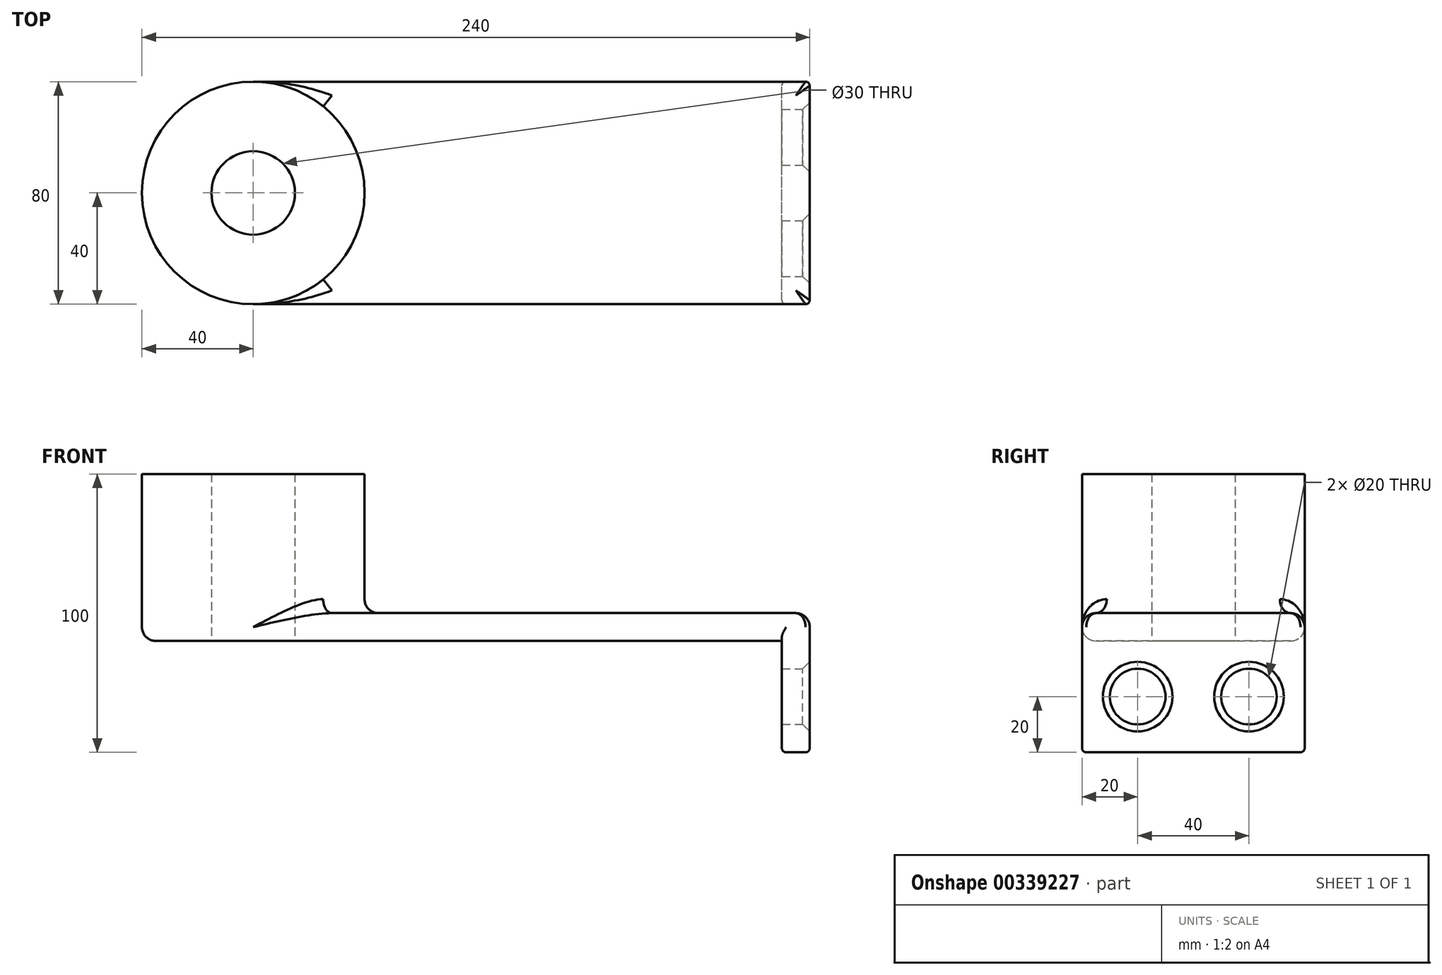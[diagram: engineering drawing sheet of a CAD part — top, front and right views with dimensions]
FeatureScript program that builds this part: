
annotation { "Feature Type Name" : "Feature", "Feature Type Description" : "" }
export const myFeature = defineFeature(function(context is Context, id is Id, definition is map)
    precondition{}
    {
        {
            var Q0;
            Q0=qCreatedBy(makeId("Top.planeOp"),FACE);
            var sketch = newSketch(context, id + "F0", { "sketchPlane" : qUnion([Q0])});
            skLineSegment(sketch, "E0.bottom", {"start": v(100, 40) * mm, "end": v(-100, 40) * mm});
            skLineSegment(sketch, "E0.top", {"start": v(100, -40) * mm, "end": v(-100, -40) * mm});
            skLineSegment(sketch, "E0.left", {"start": v(100, 40) * mm, "end": v(100, -40) * mm});
            skLineSegment(sketch, "E0.right", {"start": v(-100, 40) * mm, "end": v(-100, -40) * mm});
            skPoint(sketch, "E0.middle", {"position": v(0, 0) * mm});
            skCircle(sketch, "E1", {"center": v(-100, 0) * mm, "radius": 40 * mm});
            skCircle(sketch, "E2", {"center": v(-100, 0) * mm, "radius": 15 * mm});
            skSolve(sketch);
        }
        {
            var Q0;
            Q0=makeQuery(id+"F0.imprint","IMPRINT",FACE,{"disambiguationData":[TD([[makeQuery(id+"F0.imprint","IMPRINT",EDGE,{"derivedFrom":sQuery(id+"F0.wireOp",EDGE,"E0.bottom")}),1.0]])]});
            var Q1;
            {var subQ1=sQuery(id+"F0.wireOp",EDGE,"E0.right");var subQ3=sQuery(id+"F0.wireOp",EDGE,"E2");var subQ4=makeQuery(id+"F0.imprint","INTERSECT",VERTEX,{"disambiguationData":[OD(0.0)],"derivedFrom":[subQ1,subQ3]});Q1=makeQuery(id+"F0.imprint","IMPRINT",FACE,{"disambiguationData":[TD([[makeQuery(id+"F0.imprint","IMPRINT",EDGE,{"disambiguationData":[TD([[subQ4,1.0]])],"derivedFrom":subQ3}),-1.0]])]});}
            var Q2;
            {var subQ1=sQuery(id+"F0.wireOp",EDGE,"E0.right");var subQ3=sQuery(id+"F0.wireOp",EDGE,"E2");var subQ4=makeQuery(id+"F0.imprint","INTERSECT",VERTEX,{"disambiguationData":[OD(0.0)],"derivedFrom":[subQ1,subQ3]});Q2=makeQuery(id+"F0.imprint","IMPRINT",FACE,{"disambiguationData":[TD([[makeQuery(id+"F0.imprint","IMPRINT",EDGE,{"disambiguationData":[TD([[subQ4,-1.0]])],"derivedFrom":subQ3}),-1.0]])]});}
            extrude(context, id + "F1", {"entities" : qUnion([Q0, Q1, Q2]), "depth" : 10 * mm});
        }
        {
            var Q0;
            Q0=makeQuery(id+"F1.opExtrude","SWEPT_FACE",FACE,{"disambiguationData":[OSD([sQuery(id+"F0.wireOp",EDGE,"E0.left")])]});
            var sketch = newSketch(context, id + "F2", { "sketchPlane" : qUnion([Q0])});
            skLineSegment(sketch, "E3.bottom", {"start": v(-40, 10) * mm, "end": v(40, 10) * mm});
            skLineSegment(sketch, "E3.top", {"start": v(-40, -40) * mm, "end": v(40, -40) * mm});
            skLineSegment(sketch, "E3.left", {"start": v(-40, 10) * mm, "end": v(-40, -40) * mm});
            skLineSegment(sketch, "E3.right", {"start": v(40, 10) * mm, "end": v(40, -40) * mm});
            skCircle(sketch, "E4", {"center": v(-20, -20) * mm, "radius": 10 * mm});
            skCircle(sketch, "E5", {"center": v(20, -20) * mm, "radius": 10 * mm});
            skLineSegment(sketch, "E6", {"start": v(0, -40) * mm, "end": v(0, 10) * mm, "construction": true});
            skSolve(sketch);
        }
        {
            var Q0;
            Q0 = qSketchRegion(id + "F2", true);
            extrude(context, id + "F3", {"entities" : qUnion([Q0]), "operationType" : NewBodyOperationType.ADD, "oppositeDirection" : true, "depth" : 10 * mm});
        }
        {
            var Q0;
            {var subQ1=sQuery(id+"F0.wireOp",EDGE,"E0.right");var subQ3=sQuery(id+"F0.wireOp",EDGE,"E2");var subQ4=makeQuery(id+"F0.imprint","INTERSECT",VERTEX,{"disambiguationData":[OD(0.0)],"derivedFrom":[subQ1,subQ3]});Q0=makeQuery(id+"F0.imprint","IMPRINT",FACE,{"disambiguationData":[TD([[makeQuery(id+"F0.imprint","IMPRINT",EDGE,{"disambiguationData":[TD([[subQ4,1.0]])],"derivedFrom":subQ3}),-1.0]])]});}
            var Q1;
            {var subQ1=sQuery(id+"F0.wireOp",EDGE,"E0.right");var subQ3=sQuery(id+"F0.wireOp",EDGE,"E2");var subQ4=makeQuery(id+"F0.imprint","INTERSECT",VERTEX,{"disambiguationData":[OD(0.0)],"derivedFrom":[subQ1,subQ3]});Q1=makeQuery(id+"F0.imprint","IMPRINT",FACE,{"disambiguationData":[TD([[makeQuery(id+"F0.imprint","IMPRINT",EDGE,{"disambiguationData":[TD([[subQ4,-1.0]])],"derivedFrom":subQ3}),-1.0]])]});}
            extrude(context, id + "F4", {"entities" : qUnion([Q0, Q1]), "operationType" : NewBodyOperationType.ADD, "depth" : 60 * mm});
        }
        {
            var Q0;
            Q0=makeQuery(id+"F1.opExtrude","CAP_EDGE",EDGE,{"disambiguationData":[OSD([sQuery(id+"F0.wireOp",EDGE,"E0.left")])],"isStart":false});
            var Q1;
            {var subQ0=sQuery(id+"F0.wireOp",EDGE,"E1");Q1=makeQuery(id+"F4.boolean.opBoolean","INTERSECT",EDGE,{"derivedFrom":[makeQuery(id+"F1.opExtrude","CAP_FACE",FACE,{"disambiguationData":[OSD([sQuery(id+"F0.wireOp",EDGE,"E0.bottom"),sQuery(id+"F0.wireOp",EDGE,"E0.top"),sQuery(id+"F0.wireOp",EDGE,"E0.left"),subQ0,sQuery(id+"F0.wireOp",EDGE,"E2")])],"isStart":false}),makeQuery(id+"F4.opExtrude","SWEPT_FACE",FACE,{"disambiguationData":[OSD([subQ0])]})]});}
            var Q2;
            Q2=makeQuery(id+"F1.opExtrude","CAP_EDGE",EDGE,{"disambiguationData":[OSD([sQuery(id+"F0.wireOp",EDGE,"E0.top")])],"isStart":false});
            var Q3;
            Q3=makeQuery(id+"F1.opExtrude","CAP_EDGE",EDGE,{"disambiguationData":[OSD([sQuery(id+"F0.wireOp",EDGE,"E0.bottom")])],"isStart":false});
            var Q4;
            Q4=makeQuery(id+"F1.opExtrude","CAP_EDGE",EDGE,{"disambiguationData":[OSD([sQuery(id+"F0.wireOp",EDGE,"E0.top")])],"isStart":true});
            var Q5;
            Q5=makeQuery(id+"F1.opExtrude","CAP_EDGE",EDGE,{"disambiguationData":[OSD([sQuery(id+"F0.wireOp",EDGE,"E0.bottom")])],"isStart":true});
            fillet(context, id + "F5", {"entities" : qUnion([Q0, Q1, Q2, Q3, Q4, Q5]), "radius" : 5 * mm, "tangentPropagation" : true, "allowEdgeOverflow" : false});
        }
        {
            var Q0;
            Q0=makeQuery(id+"F3.boolean.opBoolean","MERGE",EDGE,{"derivedFrom":[makeQuery(id+"F1.opExtrude","SWEPT_EDGE",EDGE,{"disambiguationData":[OSD([sQuery(id+"F0.wireOp",EDGE,"E0.bottom"),sQuery(id+"F0.wireOp",EDGE,"E0.left")])]}),makeQuery(id+"F3.opExtrude","CAP_EDGE",EDGE,{"disambiguationData":[OSD([sQuery(id+"F2.wireOp",EDGE,"E3.right")])],"isStart":true})]});
            var Q1;
            Q1=makeQuery(id+"F3.opExtrude","CAP_EDGE",EDGE,{"disambiguationData":[OSD([sQuery(id+"F2.wireOp",EDGE,"E3.right")])],"isStart":false});
            var Q2;
            Q2=makeQuery(id+"F3.boolean.opBoolean","MERGE",EDGE,{"derivedFrom":[makeQuery(id+"F1.opExtrude","SWEPT_EDGE",EDGE,{"disambiguationData":[OSD([sQuery(id+"F0.wireOp",EDGE,"E0.top"),sQuery(id+"F0.wireOp",EDGE,"E0.left")])]}),makeQuery(id+"F3.opExtrude","CAP_EDGE",EDGE,{"disambiguationData":[OSD([sQuery(id+"F2.wireOp",EDGE,"E3.left")])],"isStart":true})]});
            var Q3;
            Q3=makeQuery(id+"F3.opExtrude","CAP_EDGE",EDGE,{"disambiguationData":[OSD([sQuery(id+"F2.wireOp",EDGE,"E3.left")])],"isStart":false});
            var Q4;
            Q4=makeQuery(id+"F3.opExtrude","CAP_EDGE",EDGE,{"disambiguationData":[OSD([sQuery(id+"F2.wireOp",EDGE,"E3.top")])],"isStart":false});
            var Q5;
            Q5=makeQuery(id+"F3.opExtrude","SWEPT_FACE",FACE,{"disambiguationData":[OSD([sQuery(id+"F2.wireOp",EDGE,"E3.top")])]});
            fillet(context, id + "F6", {"entities" : qUnion([Q0, Q1, Q2, Q3, Q4, Q5]), "radius" : 1.5 * mm, "tangentPropagation" : true, "allowEdgeOverflow" : false});
        }
        {
            var Q0;
            Q0=makeQuery(id+"F3.opExtrude","CAP_EDGE",EDGE,{"disambiguationData":[OSD([sQuery(id+"F2.wireOp",EDGE,"E4")])],"isStart":true});
            var Q1;
            Q1=makeQuery(id+"F3.opExtrude","CAP_EDGE",EDGE,{"disambiguationData":[OSD([sQuery(id+"F2.wireOp",EDGE,"E5")])],"isStart":true});
            chamfer(context, id + "F7", {"entities" : qUnion([Q0, Q1]), "chamferType" : ChamferType.OFFSET_ANGLE, "width" : 2.5 * mm, "oppositeDirection" : false, "angle" : 45 * degree, "tangentPropagation" : true});
        }
    });
